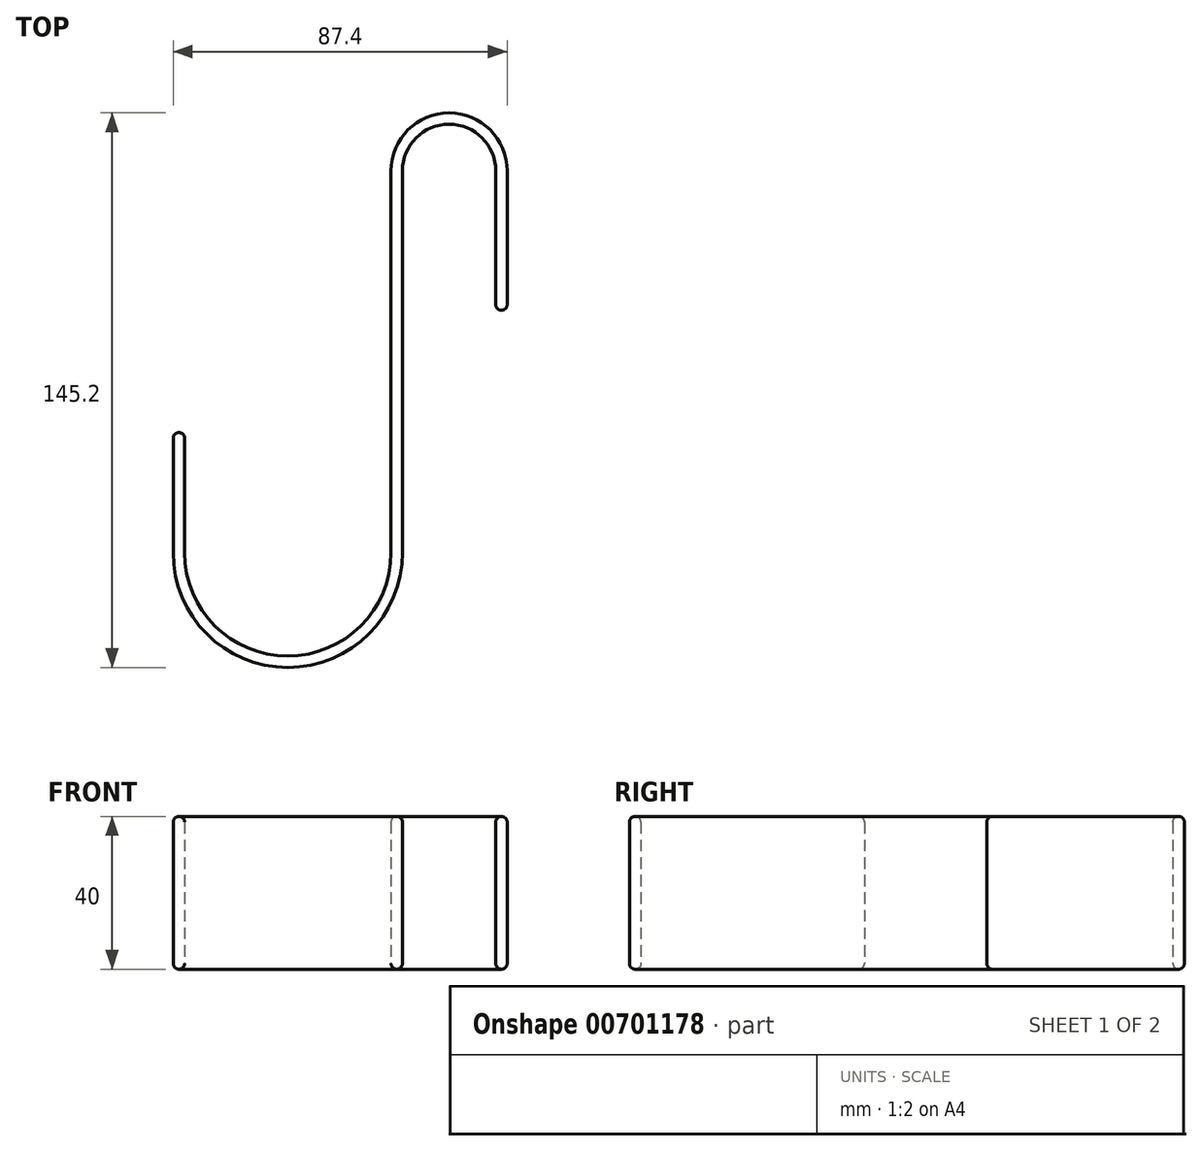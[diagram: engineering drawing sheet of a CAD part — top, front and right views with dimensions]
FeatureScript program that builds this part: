
annotation { "Feature Type Name" : "Feature", "Feature Type Description" : "" }
export const myFeature = defineFeature(function(context is Context, id is Id, definition is map)
    precondition{}
    {
        {
            var Q0;
            Q0=qCreatedBy(makeId("Top.planeOp"),FACE);
            var sketch = newSketch(context, id + "F0", { "sketchPlane" : qUnion([Q0])});
            skCircle(sketch, "E0", {"center": v(0, 0) * mm, "radius": 30 * mm, "construction": true});
            skLineSegment(sketch, "E1", {"start": v(30, 0) * mm, "end": v(30, 100) * mm});
            skLineSegment(sketch, "E2", {"start": v(54.4, 100) * mm, "end": v(54.4, 65) * mm});
            skLineSegment(sketch, "E3", {"start": v(-30, 0) * mm, "end": v(-30, 30) * mm});
            skArc(sketch, "E4", {"start": v(-30, 0) * mm, "mid": v(0, -30) * mm, "end": v(30, 0) * mm});
            skArc(sketch, "E5", {"start": v(30, 100) * mm, "mid": v(42.2, 112.2) * mm, "end": v(54.4, 100) * mm});
            skLineSegment(sketch, "E6.0", {"start": v(57.4, 100) * mm, "end": v(57.4, 65) * mm});
            skLineSegment(sketch, "E6.1", {"start": v(-27, 0) * mm, "end": v(-27, 30) * mm});
            skArc(sketch, "E6.2", {"start": v(-27, 0) * mm, "mid": v(0, -27) * mm, "end": v(27, 0) * mm});
            skLineSegment(sketch, "E6.3", {"start": v(27, 0) * mm, "end": v(27, 100) * mm});
            skArc(sketch, "E7", {"start": v(-30, 30) * mm, "mid": v(-28.5, 31.5) * mm, "end": v(-27, 30) * mm});
            skArc(sketch, "E8", {"start": v(27, 100) * mm, "mid": v(42.2, 115.2) * mm, "end": v(57.4, 100) * mm});
            skArc(sketch, "E9", {"start": v(54.4, 65) * mm, "mid": v(55.9, 63.5) * mm, "end": v(57.4, 65) * mm});
            skSolve(sketch);
        }
        {
            var Q0;
            Q0 = qSketchRegion(id + "F0", true);
            extrude(context, id + "F1", {"entities" : qUnion([Q0]), "depth" : 40 * mm, "offsetDistance" : 25 * mm});
        }
        {
            var Q0;
            Q0=makeQuery(id+"F1.opExtrude","CAP_EDGE",EDGE,{"disambiguationData":[OSD([sQuery(id+"F0.wireOp",EDGE,"E3")])],"isStart":false});
            var Q1;
            Q1=makeQuery(id+"F1.opExtrude","CAP_EDGE",EDGE,{"disambiguationData":[OSD([sQuery(id+"F0.wireOp",EDGE,"E3")])],"isStart":true});
            fillet(context, id + "F2", {"entities" : qUnion([Q0, Q1]), "radius" : 1.5 * mm, "tangentPropagation" : true, "allowEdgeOverflow" : false});
        }
    });
